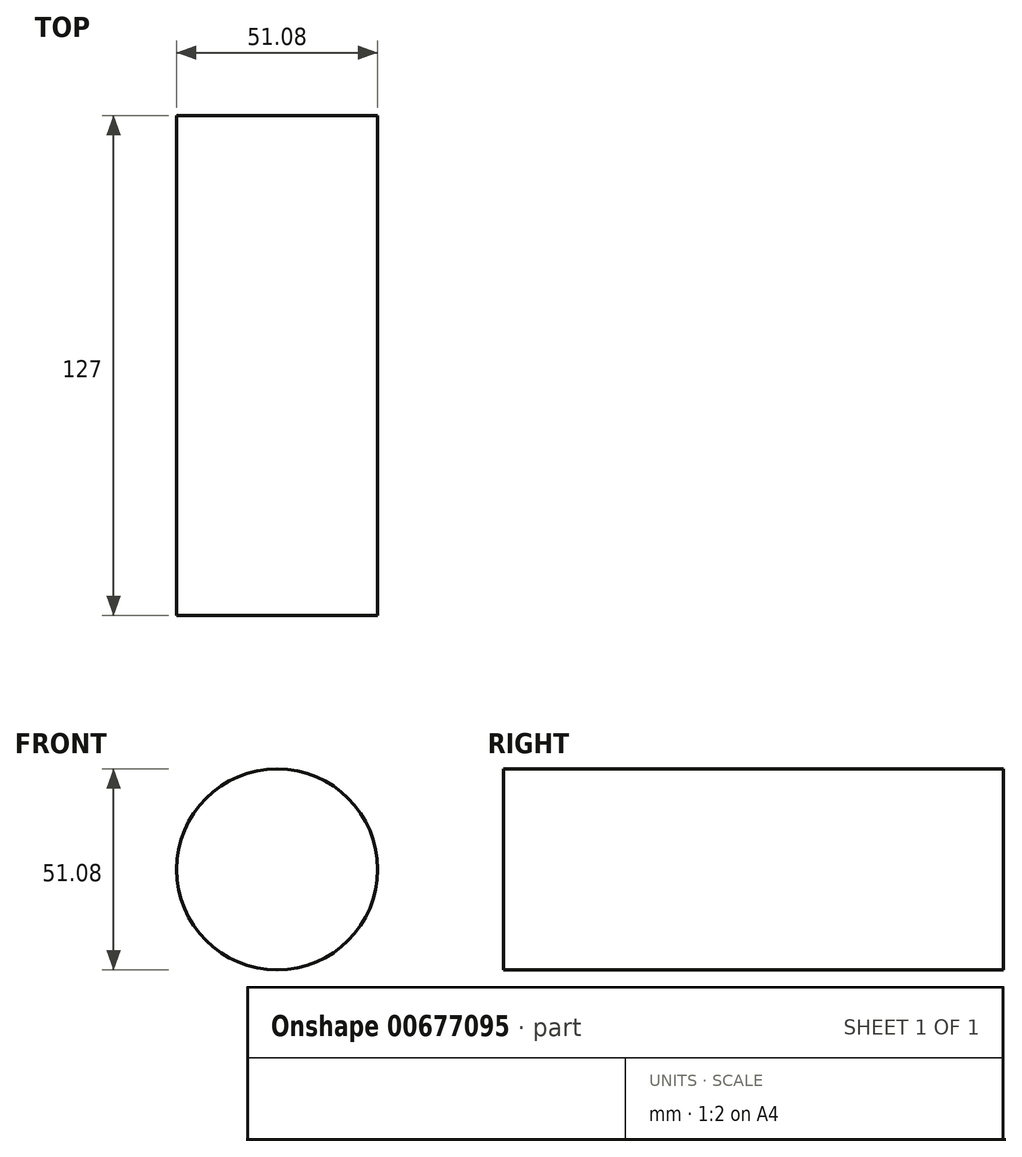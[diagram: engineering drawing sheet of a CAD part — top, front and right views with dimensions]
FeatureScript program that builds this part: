
annotation { "Feature Type Name" : "Feature", "Feature Type Description" : "" }
export const myFeature = defineFeature(function(context is Context, id is Id, definition is map)
    precondition{}
    {
        {
            var Q0;
            Q0=qCreatedBy(makeId("Front.planeOp"),FACE);
            var sketch = newSketch(context, id + "F0", { "sketchPlane" : qUnion([Q0])});
            skCircle(sketch, "E0", {"center": v(0, 0) * mm, "radius": 25.54 * mm});
            skSolve(sketch);
        }
        {
            var Q0;
            Q0=makeQuery(id+"F0.imprint","IMPRINT",FACE,{"disambiguationData":[TD([[makeQuery(id+"F0.imprint","IMPRINT",EDGE,{"derivedFrom":sQuery(id+"F0.wireOp",EDGE,"E0")}),1.0]])]});
            extrude(context, id + "F1", {"entities" : qUnion([Q0]), "endBound" : BoundingType.SYMMETRIC, "depth" : 127 * mm, "offsetDistance" : 25.4 * mm});
        }
    });
